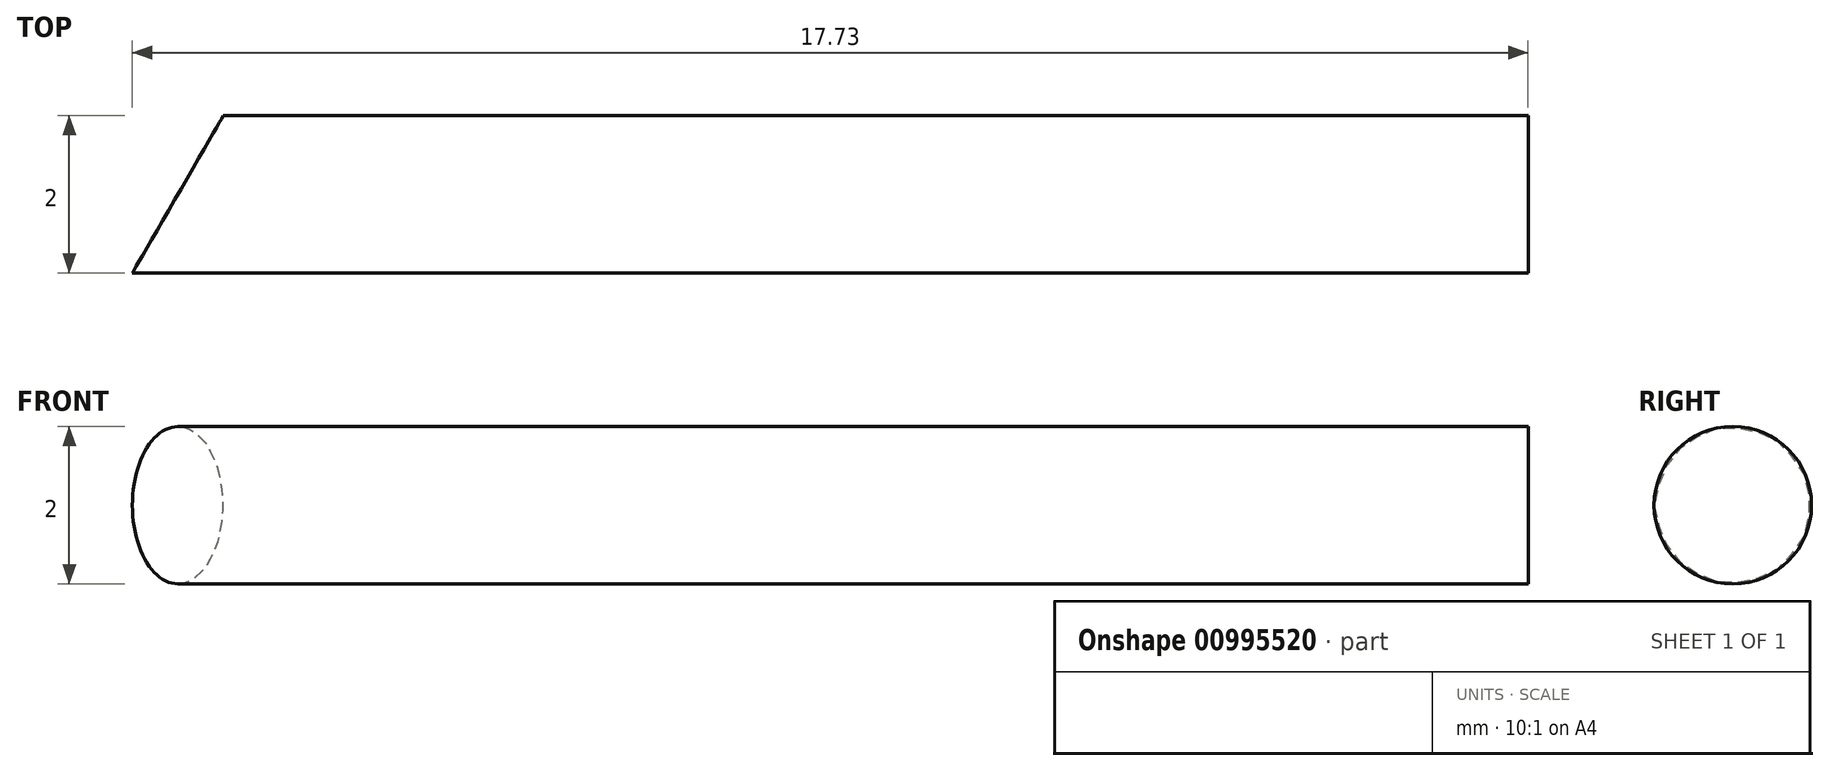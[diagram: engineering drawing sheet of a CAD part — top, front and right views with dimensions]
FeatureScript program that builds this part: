
annotation { "Feature Type Name" : "Feature", "Feature Type Description" : "" }
export const myFeature = defineFeature(function(context is Context, id is Id, definition is map)
    precondition{}
    {
        {
            var Q0;
            Q0=qCreatedBy(makeId("Top.planeOp"),FACE);
            var sketch = newSketch(context, id + "F0", { "sketchPlane" : qUnion([Q0])});
            skLineSegment(sketch, "E0", {"start": v(0, 0) * mm, "end": v(17.73, 0) * mm});
            skLineSegment(sketch, "E1", {"start": v(0, 2) * mm, "end": v(0, 0) * mm});
            skLineSegment(sketch, "E2", {"start": v(0, 2) * mm, "end": v(1.15, 2) * mm});
            skLineSegment(sketch, "E3", {"start": v(17.73, 2) * mm, "end": v(1.15, 2) * mm});
            skLineSegment(sketch, "E4", {"start": v(1.15, 2) * mm, "end": v(0, 0) * mm});
            skLineSegment(sketch, "E5", {"start": v(11.73, 2) * mm, "end": v(17.73, 2) * mm});
            skLineSegment(sketch, "E6", {"start": v(17.73, 2) * mm, "end": v(17.73, 0) * mm});
            skLineSegment(sketch, "E7", {"start": v(17.73, 0) * mm, "end": v(11.73, 0) * mm});
            skPoint(sketch, "E8.start.orphan", {"position": v(22.3, 2) * mm});
            skPoint(sketch, "E9.orphan", {"position": v(23.46, 0) * mm});
            skSolve(sketch);
        }
        {
            var Q0;
            Q0=qCreatedBy(makeId("Right.planeOp"),FACE);
            var sketch = newSketch(context, id + "F1", { "sketchPlane" : qUnion([Q0])});
            skLineSegment(sketch, "E10", {"start": v(0, 0) * mm, "end": v(0, 1) * mm});
            skLineSegment(sketch, "E11", {"start": v(0, 1) * mm, "end": v(1, 1) * mm});
            skCircle(sketch, "E12", {"center": v(1, 1) * mm, "radius": 1 * mm});
            skLineSegment(sketch, "E13", {"start": v(0, 1) * mm, "end": v(0, 2) * mm});
            skLineSegment(sketch, "E14", {"start": v(0, 2) * mm, "end": v(2, 2) * mm});
            skLineSegment(sketch, "E15", {"start": v(0, 0) * mm, "end": v(2, 0) * mm});
            skLineSegment(sketch, "E16", {"start": v(2, 2) * mm, "end": v(2, 0) * mm});
            skSolve(sketch);
        }
        {
            var Q0;
            Q0=makeQuery(id+"F0.imprint","IMPRINT",FACE,{"disambiguationData":[TD([[makeQuery(id+"F0.imprint","IMPRINT",EDGE,{"derivedFrom":sQuery(id+"F0.wireOp",EDGE,"E0")}),1.0]])]});
            extrude(context, id + "F2", {"entities" : qUnion([Q0]), "depth" : 2 * mm, "offsetDistance" : 25 * mm});
        }
        {
            var Q0;
            {var subQ0=sQuery(id+"F1.wireOp",EDGE,"E16");var subQ1=sQuery(id+"F1.wireOp",EDGE,"E12");var subQ2=makeQuery(id+"F1.imprint","INTERSECT",VERTEX,{"derivedFrom":[subQ1,subQ0]});Q0=makeQuery(id+"F1.imprint","IMPRINT",FACE,{"disambiguationData":[TD([[makeQuery(id+"F1.imprint","IMPRINT",EDGE,{"disambiguationData":[TD([[subQ2,1.0]])],"derivedFrom":subQ1}),-1.0]])]});}
            var Q1;
            {var subQ0=sQuery(id+"F1.wireOp",EDGE,"E14");var subQ1=sQuery(id+"F1.wireOp",EDGE,"E12");var subQ2=makeQuery(id+"F1.imprint","INTERSECT",VERTEX,{"derivedFrom":[subQ1,subQ0]});Q1=makeQuery(id+"F1.imprint","IMPRINT",FACE,{"disambiguationData":[TD([[makeQuery(id+"F1.imprint","IMPRINT",EDGE,{"disambiguationData":[TD([[subQ2,1.0]])],"derivedFrom":subQ1}),-1.0]])]});}
            var Q2;
            {var subQ0=sQuery(id+"F1.wireOp",EDGE,"E13");Q2=makeQuery(id+"F1.imprint","IMPRINT",FACE,{"disambiguationData":[TD([[makeQuery(id+"F1.imprint","IMPRINT",EDGE,{"derivedFrom":subQ0}),-1.0]])]});}
            var Q3;
            {var subQ0=sQuery(id+"F1.wireOp",EDGE,"E10");Q3=makeQuery(id+"F1.imprint","IMPRINT",FACE,{"disambiguationData":[TD([[makeQuery(id+"F1.imprint","IMPRINT",EDGE,{"derivedFrom":subQ0}),-1.0]])]});}
            extrude(context, id + "F3", {"entities" : qUnion([Q0, Q1, Q2, Q3]), "operationType" : NewBodyOperationType.REMOVE, "depth" : 25 * mm, "offsetDistance" : 25 * mm});
        }
        {
            var Q0;
            Q0=makeQuery(id+"F2.opExtrude","SWEPT_FACE",FACE,{"disambiguationData":[OSD([sQuery(id+"F0.wireOp",EDGE,"E4")])]});
            cPlane(context, id + "F4", {"entities" : qUnion([Q0]), "cplaneType" : CPlaneType.OFFSET, "offset" : 0 * mm, "width" : 150 * mm, "height" : 150 * mm});
        }
    });
